# Revit family: Doors - Hardware_Door_Dormakaba_TS98XEA + G-EMR Ubivis
name_source: partatom
category: Allgemeines Modell
revit_build: Autodesk Revit 2016 (Build: 20150220_1215(x64)
units: mm (PartAtom-declared; Revit-internal decimal feet)

## family parameters
Basisbauteil = Fläche
Beim Laden mit Abzugskörper schneiden = Nein
Bemaßung runder Anschluss = Durchmesser verwenden
Gemeinsam genutzt = Nein
Kann Basisbauteil für Bewehrung sein = Nein
OmniClass-Nummer = 23.30.40.11.27.11
OmniClass-Titel = Door Closers
Raumberechnungspunkt = Nein
Teiletyp = Normal

## types (1)
- Doors - Hardware_Door_Dormakaba_TS98XEA + G-EMR Ubivis
    A clearance = 75 mm
    Brand url = http://www.dormakaba.com
    Depth Jamb to Door = 0 mm  [stored 0 ft]
    Design country = Germany
    Door Closer Types = TS98XEA-G-EMR Ubivis-1_Push-Side-Door-Fixing
    EAN code = https://4048442636865
    Edition number = 1
    Front Position Closer Height = 17 mm
    Manufacturer country = Germany
    Manufacturer name = DORMA
    Material main = Aluminium
    Material secondary = Plastic
    Max Depth Jamb to Door = 0 mm  [stored 0 ft]
    NBS Reference Code = 25-38-20-20
    NBS Reference Description = Door Hardware Systems
    Nominal height = 34 mm
    Nominal width = 827 mm  [stored 2.71325 ft]
    OmniClass Code = 23-17 19 11 19 11
    OmniClass Description = Door Closers
    Opening Angle = 0.00°
    Primary Material = Aluminium-Dormakaba-Anodized Silver
    Product SKU = g-emr_ubivis_xea
    Product url = http://www.dorma.com
    Pull Side Door = TS98XEA-G-EMR Ubivis-1_Pull-Side-Door_Fixing
    Push Side Door = TS98XEA-G-EMR Ubivis-1_Push-Side-Door-Fixing
    Uniclass 1.4 Code = L41812
    Uniclass 1.4 Description = Door closers
    Uniclass 2015 Code = Pr_30_36_59_92
    Uniclass 2015 Name = Uncontrolled door closers
    Vorgabe-Ansicht = 1219 mm
    Weight Net (Kg) = 3.8

note: [stored X ft] marks values corroborated as IEEE doubles in the binary element streams (Revit-internal decimal feet)

## geometry (parser evidence)
native form markers: Blend x2, Sweep x21
no freeform markers — native parametric forms only
